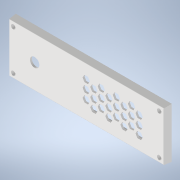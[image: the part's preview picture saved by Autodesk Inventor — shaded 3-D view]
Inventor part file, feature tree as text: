
AUTODESK INVENTOR PART (.ipt)
format: ipt  version: 2022.2 (Build 262287000, 287)  size: 363,520 bytes
history: native  units: mm
features: reference x8, extrude x5, sketch x5, other x4, projected_geometry x3, pattern_linear x1, fillet x1
ambient origin geometry x8: Origin, YZ Plane, XZ Plane, XY Plane, X Axis, Y Axis, Z Axis, Center Point
bodies: Solid1 (feature_tree)
feature tree (27):
  extrude  "Extrusion1"  Depth=4.5mm
  extrude  "Extrusion4"  TaperAngle=0.0deg  [1 undecoded]
  extrude  "Extrusion5"  Depth=5.0mm
  extrude  "Extrusion6"  Depth=2.0mm
  pattern_linear  "Rectangular Pattern1"  Spacing1=122.95014mm  [1 undecoded]
  extrude  "Extrusion7"  Depth=0.5mm
  fillet  "Fillet1"  Radius=7.0mm
  sketch  "Sketch1"  dims[d0=6.0mm d1=-0.872665mm d21=4.5mm d22=-4.363323mm]
  reference  "Reference1"
  reference  "Reference2"
  sketch  "Sketch4"  dims[d26=0.0mm d27=0.0mm d30=0.0mm d31=0.0mm]
  projected_geometry  "Projected Loop2"
  sketch  "Sketch5"  dims[d32=40.0mm d34=12.0mm d35=5.0mm]
  reference  "Reference25"
  reference  "Reference26"
  reference  "Reference27"
  reference  "Reference28"
  reference  "Reference29"
  reference  "Reference30"
  sketch  "Sketch6"  dims[d36=5.0mm d37=2.0mm]
  projected_geometry  "Projected Loop3"
  sketch  "Sketch7"  dims[d39=38.950136mm d40=122.95014mm d41=61.47507mm d42=30.0mm d44=7.0mm d46=19.475068mm d47=7.5mm d49=38.950136mm d50=19.475068mm d51=122.95014mm d52=20.49169mm d53=0.0mm d54=0.0mm d55=0.5mm]
  projected_geometry  "Projected Loop4"
  other  "<userpath>\Desktop\Jetson-Nano-2GB-Case\A.iam"
  other  "A.iam"
  other  "A-02:1"
  other  "A-01:1"
note: 2 required parameter values undecoded (feature->parameter linkage not recoverable at this tier; creation-order binding heuristic only, values carry confidence <= 0.55)
